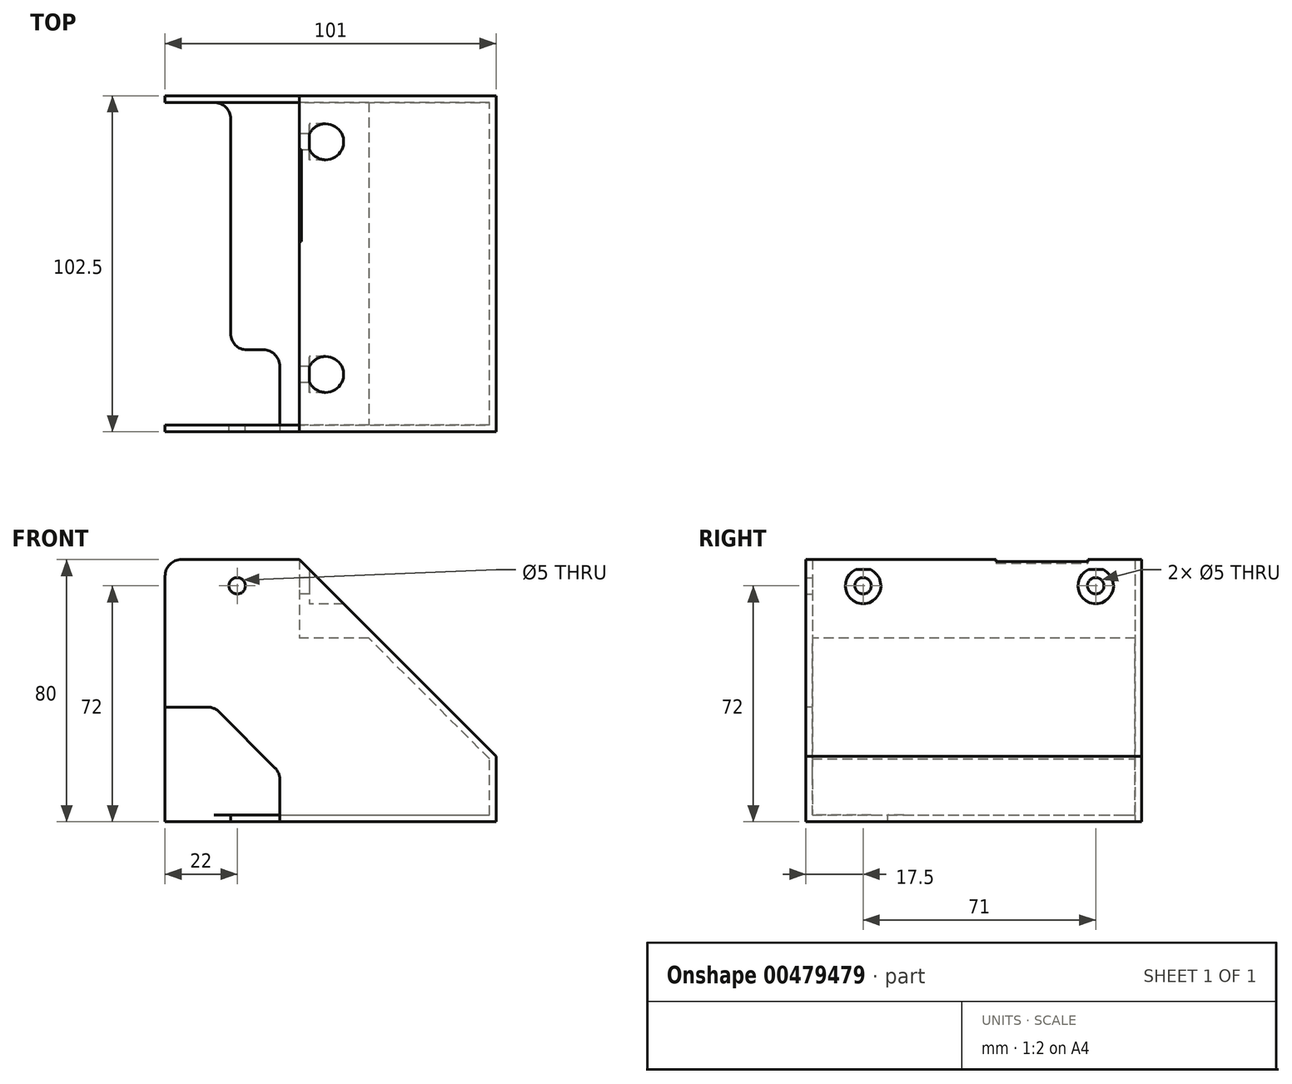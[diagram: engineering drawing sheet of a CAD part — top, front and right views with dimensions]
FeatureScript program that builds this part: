
annotation { "Feature Type Name" : "Feature", "Feature Type Description" : "" }
export const myFeature = defineFeature(function(context is Context, id is Id, definition is map)
    precondition{}
    {
        {
            var Q0;
            Q0=qCreatedBy(makeId("Front.planeOp"),FACE);
            var sketch = newSketch(context, id + "F0", { "sketchPlane" : qUnion([Q0])});
            skLineSegment(sketch, "E0", {"start": v(0, 0) * mm, "end": v(101, 0) * mm});
            skLineSegment(sketch, "E1", {"start": v(101, 0) * mm, "end": v(101, 20) * mm});
            skLineSegment(sketch, "E2", {"start": v(101, 20) * mm, "end": v(41, 80) * mm});
            skLineSegment(sketch, "E3", {"start": v(41, 80) * mm, "end": v(0, 80) * mm});
            skLineSegment(sketch, "E4", {"start": v(0, 80) * mm, "end": v(0, 0) * mm});
            skSolve(sketch);
        }
        {
            var Q0;
            Q0 = qSketchRegion(id + "F0", true);
            extrude(context, id + "F1", {"entities" : qUnion([Q0]), "depth" : 102.5 * mm});
        }
        {
            var Q0;
            Q0=makeQuery(id+"F1.opExtrude","SWEPT_FACE",FACE,{"disambiguationData":[OSD([sQuery(id+"F0.wireOp",EDGE,"E4")])]});
            var Q1;
            Q1=makeQuery(id+"F1.opExtrude","SWEPT_FACE",FACE,{"disambiguationData":[OSD([sQuery(id+"F0.wireOp",EDGE,"E3")])]});
            shell(context, id + "F2", {"entities" : qUnion([Q0, Q1]), "thickness" : 2 * mm});
        }
        {
            var Q0;
            Q0=makeQuery(id+"F2.opShell","OFFSET_FACE",FACE,{"disambiguationData":[OSD([sQuery(id+"F0.wireOp",EDGE,"E0")])]});
            var sketch = newSketch(context, id + "F3", { "sketchPlane" : qUnion([Q0])});
            skLineSegment(sketch, "E5.bottom", {"start": v(0, -2) * mm, "end": v(41, -2) * mm});
            skLineSegment(sketch, "E5.top", {"start": v(0, -100.5) * mm, "end": v(41, -100.5) * mm});
            skLineSegment(sketch, "E5.left", {"start": v(0, -2) * mm, "end": v(0, -100.5) * mm});
            skLineSegment(sketch, "E5.right", {"start": v(41, -2) * mm, "end": v(41, -100.5) * mm});
            skSolve(sketch);
        }
        {
            var Q0;
            Q0 = qSketchRegion(id + "F3", true);
            extrude(context, id + "F4", {"entities" : qUnion([Q0]), "operationType" : NewBodyOperationType.REMOVE, "endBound" : BoundingType.THROUGH_ALL, "depth" : 25 * mm});
        }
        {
            var Q0;
            Q0=makeQuery(id+"F4.boolean.opBoolean","COPY",FACE,{"derivedFrom":makeQuery(id+"F4.opExtrude","SWEPT_FACE",FACE,{"disambiguationData":[OSD([sQuery(id+"F3.wireOp",EDGE,"E5.right")])]})});
            var sketch = newSketch(context, id + "F5", { "sketchPlane" : qUnion([Q0])});
            skLineSegment(sketch, "E6.bottom", {"start": v(2, 80) * mm, "end": v(100.5, 80) * mm});
            skLineSegment(sketch, "E6.top", {"start": v(2, 56) * mm, "end": v(100.5, 56) * mm});
            skLineSegment(sketch, "E6.left", {"start": v(2, 80) * mm, "end": v(2, 56) * mm});
            skLineSegment(sketch, "E6.right", {"start": v(100.5, 80) * mm, "end": v(100.5, 56) * mm});
            skSolve(sketch);
        }
        {
            var Q0;
            Q0 = qSketchRegion(id + "F5", true);
            var Q1;
            Q1=makeQuery(id+"F1.opExtrude","SWEPT_FACE",FACE,{"disambiguationData":[OSD([sQuery(id+"F0.wireOp",EDGE,"E2")])]});
            extrude(context, id + "F6", {"entities" : qUnion([Q0]), "operationType" : NewBodyOperationType.ADD, "endBound" : BoundingType.UP_TO_SURFACE, "oppositeDirection" : true, "endBoundEntityFace" : qUnion([Q1]), "depth" : 25 * mm});
        }
        {
            var Q0;
            Q0=makeQuery(id+"F6.boolean.opBoolean","MERGE",FACE,{"derivedFrom":[makeQuery(id+"F4.boolean.opBoolean","COPY",FACE,{"derivedFrom":makeQuery(id+"F4.opExtrude","SWEPT_FACE",FACE,{"disambiguationData":[OSD([sQuery(id+"F3.wireOp",EDGE,"E5.right")])]})}),makeQuery(id+"F6.opExtrude","CAP_FACE",FACE,{"disambiguationData":[OSD([sQuery(id+"F5.wireOp",EDGE,"E6.bottom"),sQuery(id+"F5.wireOp",EDGE,"E6.top"),sQuery(id+"F5.wireOp",EDGE,"E6.left"),sQuery(id+"F5.wireOp",EDGE,"E6.right")])],"isStart":true})]});
            var sketch = newSketch(context, id + "F7", { "sketchPlane" : qUnion([Q0])});
            skPoint(sketch, "E7", {"position": v(85, 72) * mm});
            skPoint(sketch, "E8", {"position": v(14, 72) * mm});
            skSolve(sketch);
        }
        {
            var Q0;
            Q0=sQuery(id+"F7.wireOp",VERTEX,"E7");
            var Q1;
            Q1=sQuery(id+"F7.wireOp",VERTEX,"E8");
            var Q2;
            Q2=makeQuery(id+"F1.opExtrude","SWEPT_BODY",BODY,{"disambiguationData":[OSD([sQuery(id+"F0.wireOp",EDGE,"E0"),sQuery(id+"F0.wireOp",EDGE,"E1"),sQuery(id+"F0.wireOp",EDGE,"E2"),sQuery(id+"F0.wireOp",EDGE,"E3"),sQuery(id+"F0.wireOp",EDGE,"E4")])]});
            hole(context, id + "F8", {"style" : HoleStyle.SIMPLE, "endStyle" : HoleEndStyle.THROUGH, "holeDiameter" : 5 * mm, "isTappedThrough" : true, "tappedDepth" : 12 * mm, "tapClearance" : 3, "startFromSketch" : true, "locations" : qUnion([Q0, Q1]), "scope" : qUnion([Q2])});
        }
        {
            var Q0;
            Q0=makeQuery(id+"F2.opShell","OFFSET_FACE",FACE,{"disambiguationData":[OSD([sQuery(id+"F0.wireOp",EDGE,"E2")])]});
            var sketch = newSketch(context, id + "F9", { "sketchPlane" : qUnion([Q0])});
            skLineSegment(sketch, "E9.bottom", {"start": v(16.4, 26.75) * mm, "end": v(44.4, 26.75) * mm});
            skLineSegment(sketch, "E9.top", {"start": v(16.4, 75.75) * mm, "end": v(44.4, 75.75) * mm});
            skLineSegment(sketch, "E9.left", {"start": v(16.4, 26.75) * mm, "end": v(16.4, 75.75) * mm});
            skLineSegment(sketch, "E9.right", {"start": v(44.4, 26.75) * mm, "end": v(44.4, 75.75) * mm});
            skLineSegment(sketch, "E10", {"start": v(30.4, 26.75) * mm, "end": v(30.4, 75.75) * mm, "construction": true});
            skLineSegment(sketch, "E11", {"start": v(44.4, 51.25) * mm, "end": v(16.4, 51.25) * mm, "construction": true});
            skSolve(sketch);
        }
        {
            var Q0;
            Q0 = qSketchRegion(id + "F9", true);
            extrude(context, id + "F10", {"entities" : qUnion([Q0]), "operationType" : NewBodyOperationType.REMOVE, "endBound" : BoundingType.THROUGH_ALL, "oppositeDirection" : true, "depth" : 25 * mm});
        }
        {
            var Q0;
            {var subQ0=sQuery(id+"F0.wireOp",EDGE,"E4");var subQ1=sQuery(id+"F0.wireOp",EDGE,"E3");var subQ2=sQuery(id+"F0.wireOp",EDGE,"E2");var subQ3=sQuery(id+"F0.wireOp",EDGE,"E1");var subQ4=sQuery(id+"F0.wireOp",EDGE,"E0");Q0=makeQuery(id+"F4.boolean.opBoolean","MERGE",FACE,{"derivedFrom":[makeQuery(id+"F2.opShell","OFFSET_FACE",FACE,{"disambiguationData":[OSD([subQ4,subQ3,subQ2,subQ1,subQ0]),TDD([makeQuery(id+"F1.opExtrude","CAP_FACE",FACE,{"disambiguationData":[OSD([subQ4,subQ3,subQ2,subQ1,subQ0])],"isStart":false})])]}),makeQuery(id+"F4.opExtrude","SWEPT_FACE",FACE,{"disambiguationData":[OSD([sQuery(id+"F3.wireOp",EDGE,"E5.top")])]})]});}
            var sketch = newSketch(context, id + "F11", { "sketchPlane" : qUnion([Q0])});
            skPoint(sketch, "E12", {"position": v(-22, 72) * mm});
            skSolve(sketch);
        }
        {
            var Q0;
            Q0=sQuery(id+"F11.wireOp",VERTEX,"E12");
            var Q1;
            Q1=makeQuery(id+"F1.opExtrude","SWEPT_BODY",BODY,{"disambiguationData":[OSD([sQuery(id+"F0.wireOp",EDGE,"E0"),sQuery(id+"F0.wireOp",EDGE,"E1"),sQuery(id+"F0.wireOp",EDGE,"E2"),sQuery(id+"F0.wireOp",EDGE,"E3"),sQuery(id+"F0.wireOp",EDGE,"E4")])]});
            hole(context, id + "F12", {"style" : HoleStyle.SIMPLE, "endStyle" : HoleEndStyle.THROUGH, "holeDiameter" : 5 * mm, "isTappedThrough" : true, "tappedDepth" : 12 * mm, "tapClearance" : 3, "startFromSketch" : true, "locations" : qUnion([Q0]), "scope" : qUnion([Q1])});
        }
        {
            var Q0;
            Q0=makeQuery(id+"F1.opExtrude","SWEPT_FACE",FACE,{"disambiguationData":[OSD([sQuery(id+"F0.wireOp",EDGE,"E2")])]});
            var sketch = newSketch(context, id + "F13", { "sketchPlane" : qUnion([Q0])});
            skPoint(sketch, "E13", {"position": v(10.4, -51.75) * mm});
            skPoint(sketch, "E14", {"position": v(50.4, -51.75) * mm});
            skLineSegment(sketch, "E15", {"start": v(30.4, -75.75) * mm, "end": v(30.4, -26.75) * mm, "construction": true});
            skSolve(sketch);
        }
        {
            var Q0;
            Q0=sQuery(id+"F13.wireOp",VERTEX,"E13");
            var Q1;
            Q1=sQuery(id+"F13.wireOp",VERTEX,"E14");
            var Q2;
            Q2=makeQuery(id+"F1.opExtrude","SWEPT_BODY",BODY,{"disambiguationData":[OSD([sQuery(id+"F0.wireOp",EDGE,"E0"),sQuery(id+"F0.wireOp",EDGE,"E1"),sQuery(id+"F0.wireOp",EDGE,"E2"),sQuery(id+"F0.wireOp",EDGE,"E3"),sQuery(id+"F0.wireOp",EDGE,"E4")])]});
            hole(context, id + "F14", {"style" : HoleStyle.SIMPLE, "endStyle" : HoleEndStyle.BLIND, "holeDiameter" : 3 * mm, "holeDepth" : 12 * mm, "isTappedThrough" : true, "tappedDepth" : 12 * mm, "tapClearance" : 3, "startFromSketch" : true, "locations" : qUnion([Q0, Q1]), "scope" : qUnion([Q2])});
        }
        {
            var Q0;
            Q0=makeQuery(id+"F1.opExtrude","SWEPT_FACE",FACE,{"disambiguationData":[OSD([sQuery(id+"F0.wireOp",EDGE,"E4")])]});
            var sketch = newSketch(context, id + "F15", { "sketchPlane" : qUnion([Q0])});
            skLineSegment(sketch, "E16.bottom", {"start": v(2, 2) * mm, "end": v(100.5, 2) * mm});
            skLineSegment(sketch, "E16.top", {"start": v(2, 0) * mm, "end": v(100.5, 0) * mm});
            skLineSegment(sketch, "E16.left", {"start": v(2, 2) * mm, "end": v(2, 0) * mm});
            skLineSegment(sketch, "E16.right", {"start": v(100.5, 2) * mm, "end": v(100.5, 0) * mm});
            skSolve(sketch);
        }
        {
            var Q0;
            Q0 = qSketchRegion(id + "F15", true);
            extrude(context, id + "F16", {"entities" : qUnion([Q0]), "operationType" : NewBodyOperationType.REMOVE, "oppositeDirection" : true, "depth" : 20 * mm});
        }
        {
            var Q0;
            Q0=makeQuery(id+"F1.opExtrude","CAP_FACE",FACE,{"disambiguationData":[OSD([sQuery(id+"F0.wireOp",EDGE,"E0"),sQuery(id+"F0.wireOp",EDGE,"E1"),sQuery(id+"F0.wireOp",EDGE,"E2"),sQuery(id+"F0.wireOp",EDGE,"E3"),sQuery(id+"F0.wireOp",EDGE,"E4")])],"isStart":false});
            var sketch = newSketch(context, id + "F17", { "sketchPlane" : qUnion([Q0])});
            skLineSegment(sketch, "E17", {"start": v(0, 0) * mm, "end": v(0, 35) * mm});
            skLineSegment(sketch, "E18", {"start": v(15, 35) * mm, "end": v(35, 15) * mm});
            skLineSegment(sketch, "E19", {"start": v(35, 15) * mm, "end": v(35, 0) * mm});
            skLineSegment(sketch, "E20", {"start": v(35, 0) * mm, "end": v(0, 0) * mm});
            skLineSegment(sketch, "E21", {"start": v(0, 35) * mm, "end": v(15, 35) * mm});
            skSolve(sketch);
        }
        {
            var Q0;
            Q0 = qSketchRegion(id + "F17", true);
            extrude(context, id + "F18", {"entities" : qUnion([Q0]), "operationType" : NewBodyOperationType.REMOVE, "oppositeDirection" : true, "depth" : 25 * mm});
        }
        {
            var Q0;
            Q0=makeQuery(id+"F6.boolean.opBoolean","MERGE",FACE,{"derivedFrom":[makeQuery(id+"F4.boolean.opBoolean","COPY",FACE,{"derivedFrom":makeQuery(id+"F4.opExtrude","SWEPT_FACE",FACE,{"disambiguationData":[OSD([sQuery(id+"F3.wireOp",EDGE,"E5.right")])]})}),makeQuery(id+"F6.opExtrude","CAP_FACE",FACE,{"disambiguationData":[OSD([sQuery(id+"F5.wireOp",EDGE,"E6.bottom"),sQuery(id+"F5.wireOp",EDGE,"E6.top"),sQuery(id+"F5.wireOp",EDGE,"E6.left"),sQuery(id+"F5.wireOp",EDGE,"E6.right")])],"isStart":true})]});
            cPlane(context, id + "F19", {"entities" : qUnion([Q0]), "cplaneType" : CPlaneType.OFFSET, "offset" : 3 * mm, "oppositeDirection" : true, "width" : 150 * mm, "height" : 150 * mm});
        }
        {
            var Q0;
            Q0=qCreatedBy(id+"F19.planeOp",FACE);
            var sketch = newSketch(context, id + "F20", { "sketchPlane" : qUnion([Q0])});
            skCircle(sketch, "E22", {"center": v(85, 72) * mm, "radius": 5.5 * mm});
            skCircle(sketch, "E23", {"center": v(14, 72) * mm, "radius": 5.5 * mm});
            skSolve(sketch);
        }
        {
            var Q0;
            Q0 = qSketchRegion(id + "F20", true);
            extrude(context, id + "F21", {"entities" : qUnion([Q0]), "operationType" : NewBodyOperationType.REMOVE, "oppositeDirection" : true, "depth" : 25 * mm});
        }
        {
            var Q0;
            Q0=makeQuery(id+"F18.boolean.opBoolean","COPY",EDGE,{"derivedFrom":makeQuery(id+"F18.opExtrude","CAP_EDGE",EDGE,{"disambiguationData":[OSD([sQuery(id+"F17.wireOp",EDGE,"E19")])],"isStart":false})});
            var Q1;
            Q1=makeQuery(id+"F18.boolean.opBoolean","COPY",EDGE,{"derivedFrom":makeQuery(id+"F18.opExtrude","SWEPT_EDGE",EDGE,{"disambiguationData":[OSD([sQuery(id+"F17.wireOp",EDGE,"E18"),sQuery(id+"F17.wireOp",EDGE,"E19")])]})});
            var Q2;
            Q2=makeQuery(id+"F18.boolean.opBoolean","COPY",EDGE,{"derivedFrom":makeQuery(id+"F18.opExtrude","SWEPT_EDGE",EDGE,{"disambiguationData":[OSD([sQuery(id+"F17.wireOp",EDGE,"E18"),sQuery(id+"F17.wireOp",EDGE,"E21")])]})});
            var Q3;
            Q3=makeQuery(id+"F18.boolean.opBoolean","INTERSECT",EDGE,{"derivedFrom":[makeQuery(id+"F16.boolean.opBoolean","COPY",FACE,{"derivedFrom":makeQuery(id+"F16.opExtrude","CAP_FACE",FACE,{"disambiguationData":[OSD([sQuery(id+"F15.wireOp",EDGE,"E16.bottom"),sQuery(id+"F15.wireOp",EDGE,"E16.top"),sQuery(id+"F15.wireOp",EDGE,"E16.left"),sQuery(id+"F15.wireOp",EDGE,"E16.right")])],"isStart":false})}),makeQuery(id+"F18.opExtrude","CAP_FACE",FACE,{"disambiguationData":[OSD([sQuery(id+"F17.wireOp",EDGE,"E17"),sQuery(id+"F17.wireOp",EDGE,"E18"),sQuery(id+"F17.wireOp",EDGE,"E19"),sQuery(id+"F17.wireOp",EDGE,"E20"),sQuery(id+"F17.wireOp",EDGE,"E21")])],"isStart":false})]});
            var Q4;
            Q4=makeQuery(id+"F16.boolean.opBoolean","COPY",EDGE,{"derivedFrom":makeQuery(id+"F16.opExtrude","CAP_EDGE",EDGE,{"disambiguationData":[OSD([sQuery(id+"F15.wireOp",EDGE,"E16.left")])],"isStart":false})});
            var Q5;
            Q5=makeQuery(id+"F1.opExtrude","SWEPT_EDGE",EDGE,{"disambiguationData":[OSD([sQuery(id+"F0.wireOp",EDGE,"E3"),sQuery(id+"F0.wireOp",EDGE,"E4")])]});
            var Q6;
            Q6=makeQuery(id+"F2.opShell","OFFSET_EDGE",EDGE,{"disambiguationData":[OSD([sQuery(id+"F0.wireOp",EDGE,"E3"),sQuery(id+"F0.wireOp",EDGE,"E4")])]});
            var Q7;
            Q7=makeQuery(id+"F18.boolean.opBoolean","COPY",EDGE,{"derivedFrom":makeQuery(id+"F18.opExtrude","SWEPT_EDGE",EDGE,{"disambiguationData":[OSD([sQuery(id+"F0.wireOp",EDGE,"E4"),sQuery(id+"F17.wireOp",EDGE,"E17"),sQuery(id+"F17.wireOp",EDGE,"E21")])]})});
            fillet(context, id + "F22", {"entities" : qUnion([Q0, Q1, Q2, Q3, Q4, Q5, Q6, Q7]), "radius" : 5 * mm, "tangentPropagation" : true, "allowEdgeOverflow" : false});
        }
    });
